# Revit family: Indoor_Pendant Lamp_Santa&Cole_HeadHat Plate
name_source: partatom
category: Luminarias
revit_build: Autodesk Revit 2018 (Build: 20190510_1515(x64)
units: mm (PartAtom-declared; Revit-internal decimal feet)

## family parameters
Anfitrión = Cara
Compartido = No
Corte con vacíos al cargar = No
Cota de conector redondo = Diámetro de uso
Origen de luz = Sí
Punto de cálculo de habitación = No
Tipo de pieza = Normal

## types (12) — shared parameters
Archivo de red fotométrica = HATS02_500mA.IES
Assembly Instructions - CE = https://www.santacole.com
Assembly Instructions - UL = https://www.santacole.com
Cambio de temperatura de color de luz atenuada = <Ninguno>
Elevación por defecto = 1219 mm
Energy Label = https://www.santacole.com
Fabricante = Santa & Cole
Filtro de color = 16777215
Manufacturer website = http://www.santacole.com
Modelo = HeadHat Plate
Technical Information = https://www.santacole.com
URL = https://www.santacole.com
Voltaje (90-305 V) = 220 V
Ángulo de inclinación = -90.00°

## per-type parameters (varying)
| type | Carga aparente | Code | Lampshade Material | Load | Visibility_L | Visibility_M | Visibility_S |
| HeadHat Plate S - White | 8 W | HEFxx+HEL0x+HATS0x | Santa&Cole - White Matte Finish | 10 W | No | No | Sí |
| HeadHat Plate S - Berry Blue | 8 W | HEFxx+HEL0x+HATS0x | Santa&Cole - Berry Blue Metallic Matte Finish | 10 W | No | No | Sí |
| HeadHat Plate S - Truffle Brown | 8 W | HEFxx+HEL0x+HATS0x | Santa&Cole - Truffle Brown Metallic Matte Finish | 10 W | No | No | Sí |
| HeadHat Plate S - Hematite Red | 0 W | HEFxx+HEL0x+HATS0x | Santa&Cole - Hematite Red Metallic Matte Finish | 0 W | No | No | Sí |
| HeadHat Plate M - Berry Blue | 8 W | HEFxx+HEL0x+HATM0x | Santa&Cole - Berry Blue Metallic Matte Finish | 10 W | No | Sí | No |
| HeadHat Plate M - Hematite Red | 8 W | HEFxx+HEL0x+HATM0x | Santa&Cole - Hematite Red Metallic Matte Finish | 8 W | No | Sí | No |
| HeadHat Plate M - Truffle Brown | 8 W | HEFxx+HEL0x+HATM0x | Santa&Cole - Truffle Brown Metallic Matte Finish | 10 W | No | Sí | No |
| HeadHat Plate M - White | 8 W | HEFxx+HEL0x+HATM0x | Santa&Cole - White Matte Finish | 10 W | No | Sí | No |
| HeadHat Plate L - White | 8 W | HEFxx+HEL0x+HATL0x | Santa&Cole - White Matte Finish | 10 W | Sí | No | No |
| HeadHat Plate L - Truffle Brown | 8 W | HEFxx+HEL0x+HATL0x | Santa&Cole - Truffle Brown Metallic Matte Finish | 10 W | Sí | No | No |
| HeadHat Plate L - Hematite Red | 8 W | HEFxx+HEL0x+HATL0x | Santa&Cole - Hematite Red Metallic Matte Finish | 10 W | Sí | No | No |
| HeadHat Plate L - Berry Blue | 8 W | HEFxx+HEL0x+HATL0x | Santa&Cole - Berry Blue Metallic Matte Finish | 8 W | Sí | No | No |

## geometry (parser evidence)
native form markers: Blend x4, Sweep x7
no freeform markers — native parametric forms only
